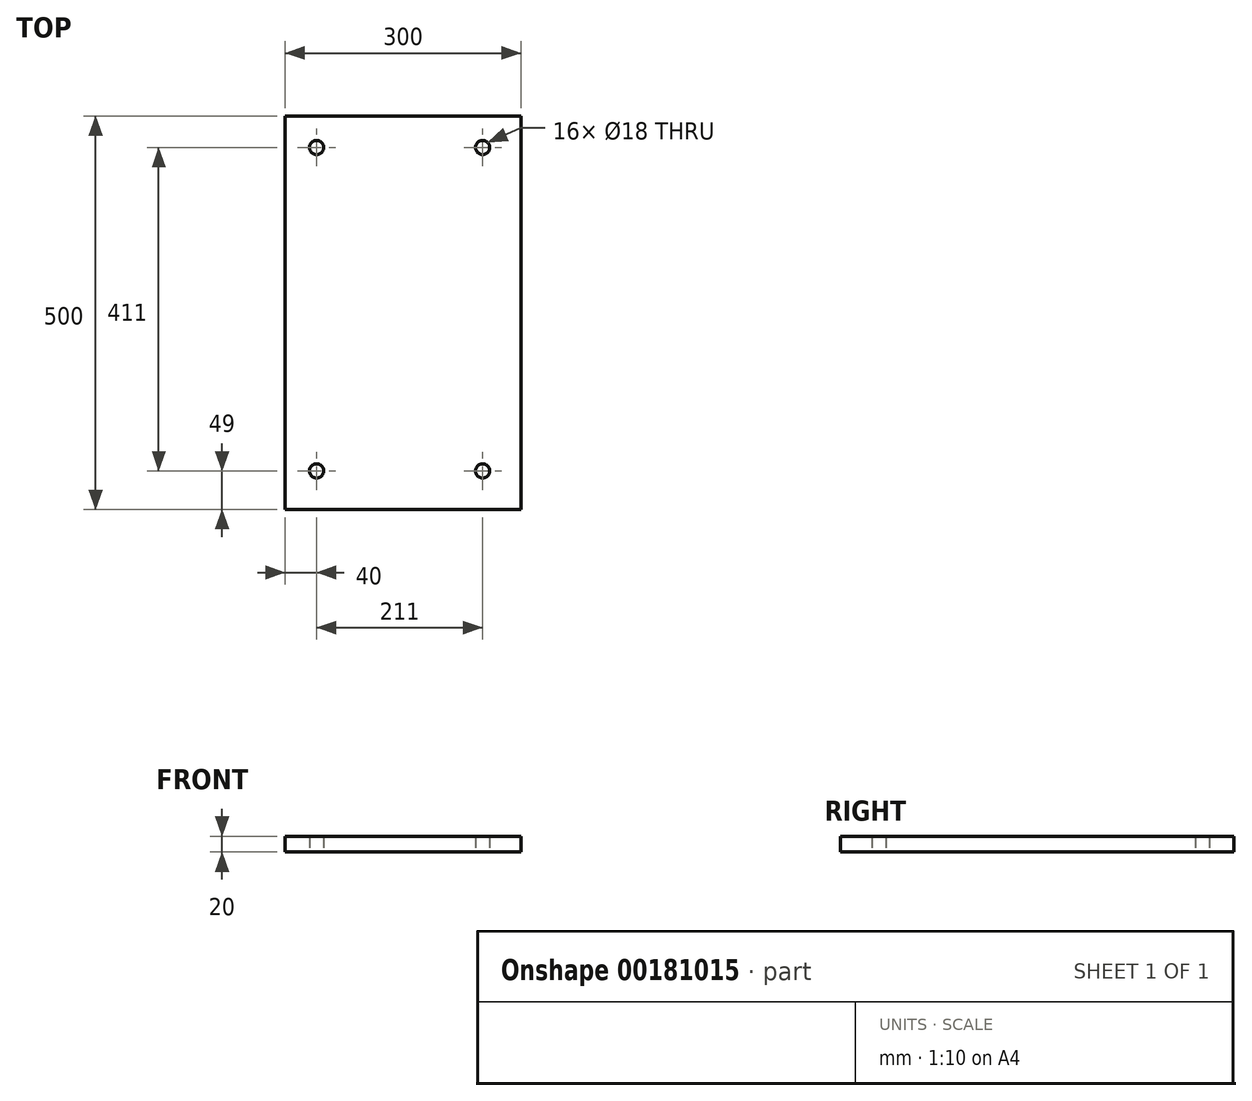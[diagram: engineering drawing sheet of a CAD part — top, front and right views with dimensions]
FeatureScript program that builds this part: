
annotation { "Feature Type Name" : "Feature", "Feature Type Description" : "" }
export const myFeature = defineFeature(function(context is Context, id is Id, definition is map)
    precondition{}
    {
        {
            var Q0;
            Q0=qCreatedBy(makeId("Top.planeOp"),FACE);
            var sketch = newSketch(context, id + "F0", { "sketchPlane" : qUnion([Q0])});
            skLineSegment(sketch, "E0.bottom", {"start": v(-150, 250) * mm, "end": v(150, 250) * mm});
            skLineSegment(sketch, "E0.top", {"start": v(-150, -250) * mm, "end": v(150, -250) * mm});
            skLineSegment(sketch, "E0.left", {"start": v(-150, 250) * mm, "end": v(-150, -250) * mm});
            skLineSegment(sketch, "E0.right", {"start": v(150, 250) * mm, "end": v(150, -250) * mm});
            skCircle(sketch, "E1", {"center": v(-110, 210) * mm, "radius": 9 * mm});
            skCircle(sketch, "E2", {"center": v(101, 210) * mm, "radius": 9 * mm});
            skCircle(sketch, "E3", {"center": v(101, -201) * mm, "radius": 9 * mm});
            skCircle(sketch, "E4", {"center": v(-110, -201) * mm, "radius": 9 * mm});
            skSolve(sketch);
        }
        {
            var Q0;
            Q0=makeQuery(id+"F0.imprint","IMPRINT",FACE,{"disambiguationData":[TD([[makeQuery(id+"F0.imprint","IMPRINT",EDGE,{"derivedFrom":sQuery(id+"F0.wireOp",EDGE,"E0.bottom")}),-1.0]])]});
            extrude(context, id + "F1", {"entities" : qUnion([Q0]), "depth" : 20 * mm});
        }
    });
